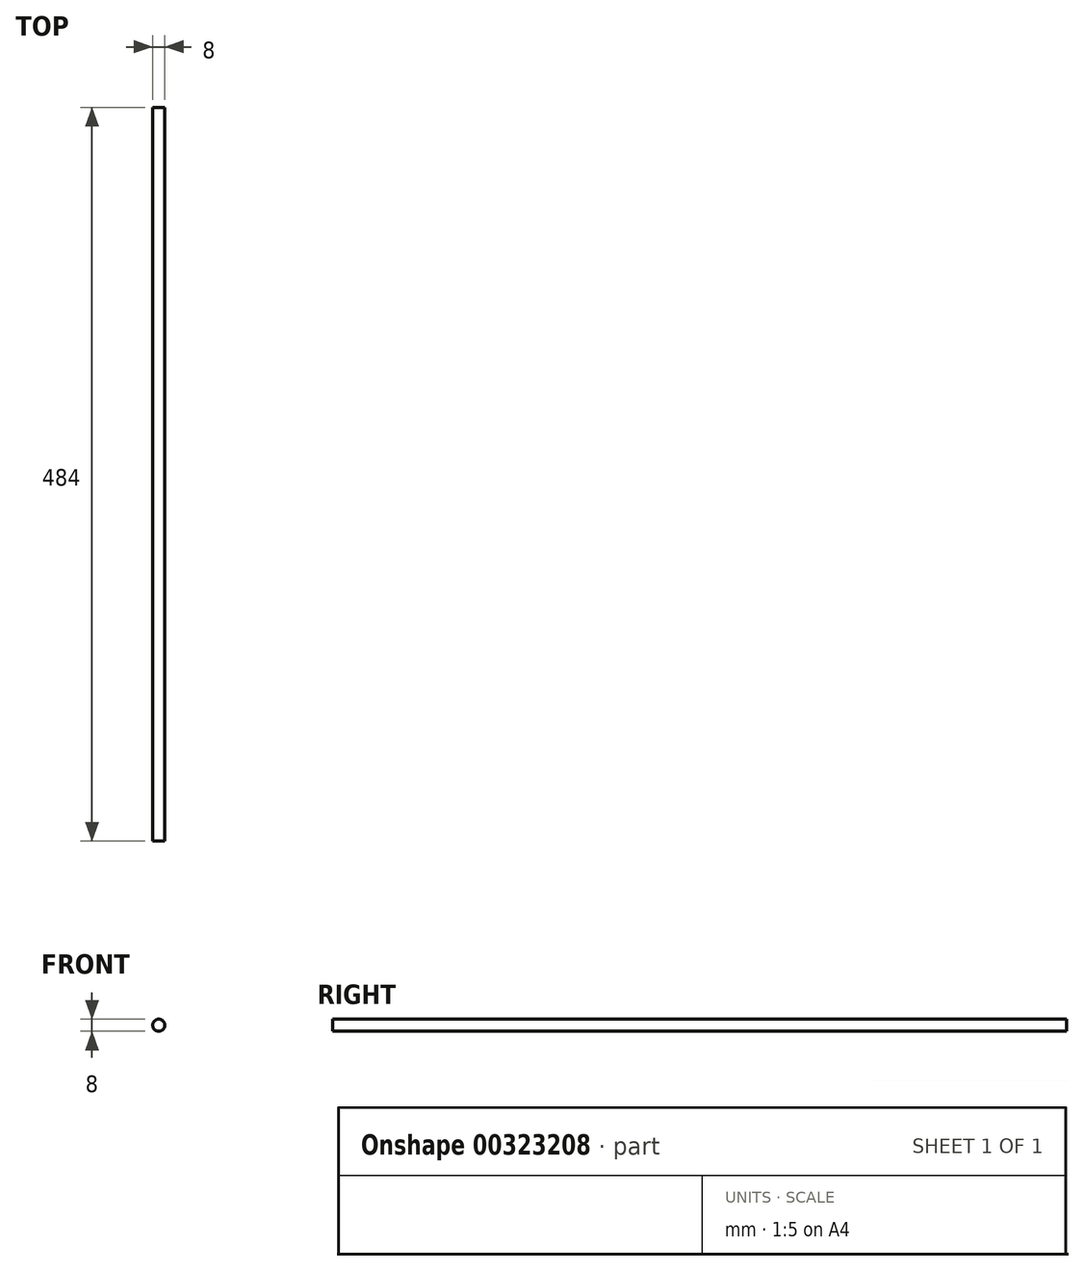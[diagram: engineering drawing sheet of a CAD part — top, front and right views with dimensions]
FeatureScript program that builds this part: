
annotation { "Feature Type Name" : "Feature", "Feature Type Description" : "" }
export const myFeature = defineFeature(function(context is Context, id is Id, definition is map)
    precondition{}
    {
        {
            var Q0;
            Q0=qCreatedBy(makeId("Front.planeOp"),FACE);
            var sketch = newSketch(context, id + "F0", { "sketchPlane" : qUnion([Q0])});
            skCircle(sketch, "E0", {"center": v(0, 0) * mm, "radius": 4 * mm});
            skSolve(sketch);
        }
        {
            var Q0;
            Q0=qSketchRegion(id+"F0",true);
            extrude(context, id + "F1", {"entities" : qUnion([Q0]), "endBound" : BoundingType.SYMMETRIC, "depth" : 484 * mm});
        }
    });
